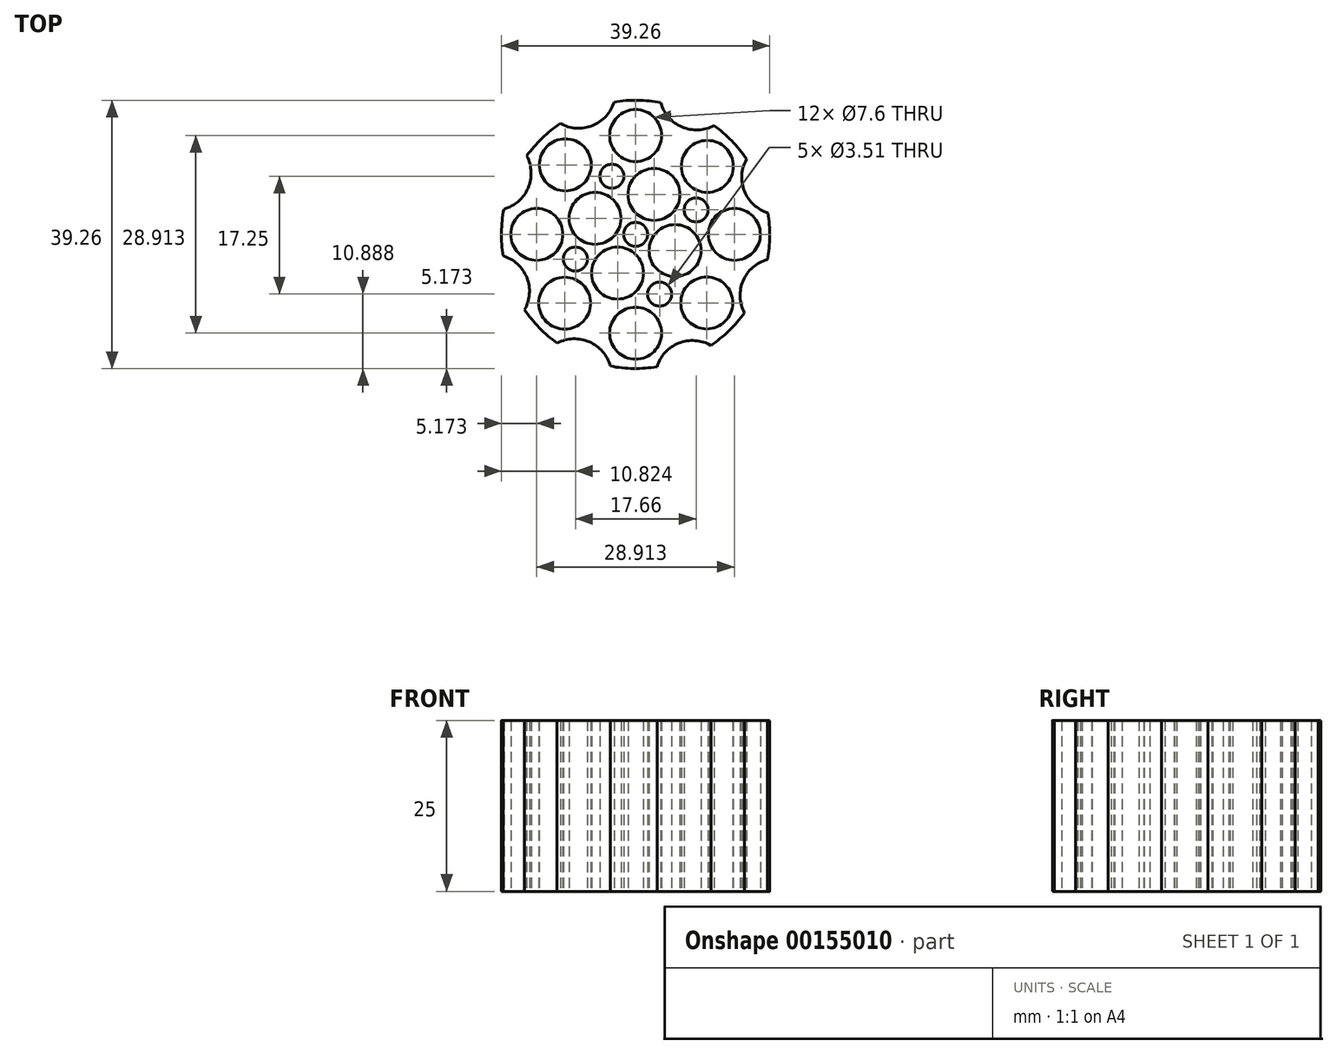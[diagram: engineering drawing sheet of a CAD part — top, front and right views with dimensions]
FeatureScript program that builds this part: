
annotation { "Feature Type Name" : "Feature", "Feature Type Description" : "" }
export const myFeature = defineFeature(function(context is Context, id is Id, definition is map)
    precondition{}
    {
        {
            var Q0;
            Q0=qCreatedBy(makeId("Top.planeOp"),FACE);
            var sketch = newSketch(context, id + "F0", { "sketchPlane" : qUnion([Q0])});
            skCircle(sketch, "E0", {"center": v(0, 14.46) * mm, "radius": 3.8 * mm});
            skCircle(sketch, "E1", {"center": v(14.46, 0) * mm, "radius": 3.8 * mm});
            skCircle(sketch, "E2", {"center": v(-14.46, 0) * mm, "radius": 3.8 * mm});
            skCircle(sketch, "E3", {"center": v(5.77, -2.38) * mm, "radius": 3.8 * mm});
            skCircle(sketch, "E4", {"center": v(10.4, -10.03) * mm, "radius": 3.8 * mm});
            skCircle(sketch, "E5", {"center": v(0, -14.46) * mm, "radius": 3.8 * mm});
            skCircle(sketch, "E6", {"center": v(-10.28, 10.17) * mm, "radius": 3.8 * mm});
            skCircle(sketch, "E7", {"center": v(10.5, 9.94) * mm, "radius": 3.8 * mm});
            skCircle(sketch, "E8", {"center": v(-5.93, 2.35) * mm, "radius": 3.8 * mm});
            skCircle(sketch, "E9", {"center": v(-10.38, -10.06) * mm, "radius": 3.8 * mm});
            skCircle(sketch, "E10", {"center": v(2.7, 5.84) * mm, "radius": 3.8 * mm});
            skCircle(sketch, "E11", {"center": v(-2.65, -5.66) * mm, "radius": 3.8 * mm});
            skArc(sketch, "E12", {"start": v(3.7, 19.28) * mm, "mid": v(0.28, 19.63) * mm, "end": v(-3.14, 19.37) * mm});
            skArc(sketch, "E13", {"start": v(3.7, 19.28) * mm, "mid": v(6.78, 15.73) * mm, "end": v(11.48, 15.92) * mm});
            skCircle(sketch, "E14", {"center": v(0, 0) * mm, "radius": 1.75 * mm});
            skCircle(sketch, "E15", {"center": v(8.85, 3.58) * mm, "radius": 1.75 * mm});
            skCircle(sketch, "E16", {"center": v(-3.47, 8.5) * mm, "radius": 1.75 * mm});
            skCircle(sketch, "E17", {"center": v(3.51, -8.74) * mm, "radius": 1.75 * mm});
            skCircle(sketch, "E18", {"center": v(-8.8, -3.6) * mm, "radius": 1.75 * mm});
            skArc(sketch, "E19.1.0", {"start": v(-11.02, 16.24) * mm, "mid": v(-6.33, 15.91) * mm, "end": v(-3.14, 19.37) * mm});
            skArc(sketch, "E19.2.0", {"start": v(-19.28, 3.7) * mm, "mid": v(-15.73, 6.78) * mm, "end": v(-15.92, 11.48) * mm});
            skArc(sketch, "E19.3.0", {"start": v(-16.24, -11.02) * mm, "mid": v(-15.91, -6.33) * mm, "end": v(-19.37, -3.14) * mm});
            skArc(sketch, "E19.4.0", {"start": v(-3.7, -19.28) * mm, "mid": v(-6.78, -15.73) * mm, "end": v(-11.48, -15.92) * mm});
            skArc(sketch, "E19.5.0", {"start": v(11.02, -16.24) * mm, "mid": v(6.33, -15.91) * mm, "end": v(3.14, -19.37) * mm});
            skArc(sketch, "E19.6.0", {"start": v(19.28, -3.7) * mm, "mid": v(15.73, -6.78) * mm, "end": v(15.92, -11.48) * mm});
            skArc(sketch, "E19.7.0", {"start": v(16.24, 11.02) * mm, "mid": v(15.91, 6.33) * mm, "end": v(19.37, 3.14) * mm});
            skArc(sketch, "E20.trimOffspring", {"start": v(-11.02, 16.24) * mm, "mid": v(-13.68, 14.08) * mm, "end": v(-15.92, 11.48) * mm});
            skArc(sketch, "E21.trimOffspring", {"start": v(-19.28, 3.7) * mm, "mid": v(-19.63, 0.28) * mm, "end": v(-19.37, -3.14) * mm});
            skArc(sketch, "E22.trimOffspring", {"start": v(-16.24, -11.02) * mm, "mid": v(-14.08, -13.68) * mm, "end": v(-11.48, -15.92) * mm});
            skArc(sketch, "E23.trimOffspring", {"start": v(-3.7, -19.28) * mm, "mid": v(-0.28, -19.63) * mm, "end": v(3.14, -19.37) * mm});
            skArc(sketch, "E24.trimOffspring", {"start": v(11.02, -16.24) * mm, "mid": v(13.68, -14.08) * mm, "end": v(15.92, -11.48) * mm});
            skArc(sketch, "E25.trimOffspring", {"start": v(19.28, -3.7) * mm, "mid": v(19.63, -0.28) * mm, "end": v(19.37, 3.14) * mm});
            skArc(sketch, "E26.trimOffspring", {"start": v(16.24, 11.02) * mm, "mid": v(14.08, 13.68) * mm, "end": v(11.48, 15.92) * mm});
            skSolve(sketch);
        }
        {
            var Q0;
            Q0=makeQuery(id+"F0.imprint","IMPRINT",FACE,{"disambiguationData":[TD([[makeQuery(id+"F0.imprint","IMPRINT",EDGE,{"derivedFrom":sQuery(id+"F0.wireOp",EDGE,"E0")}),-1.0]])]});
            extrude(context, id + "F1", {"entities" : qUnion([Q0]), "depth" : 25 * mm, "offsetDistance" : 25 * mm});
        }
    });
